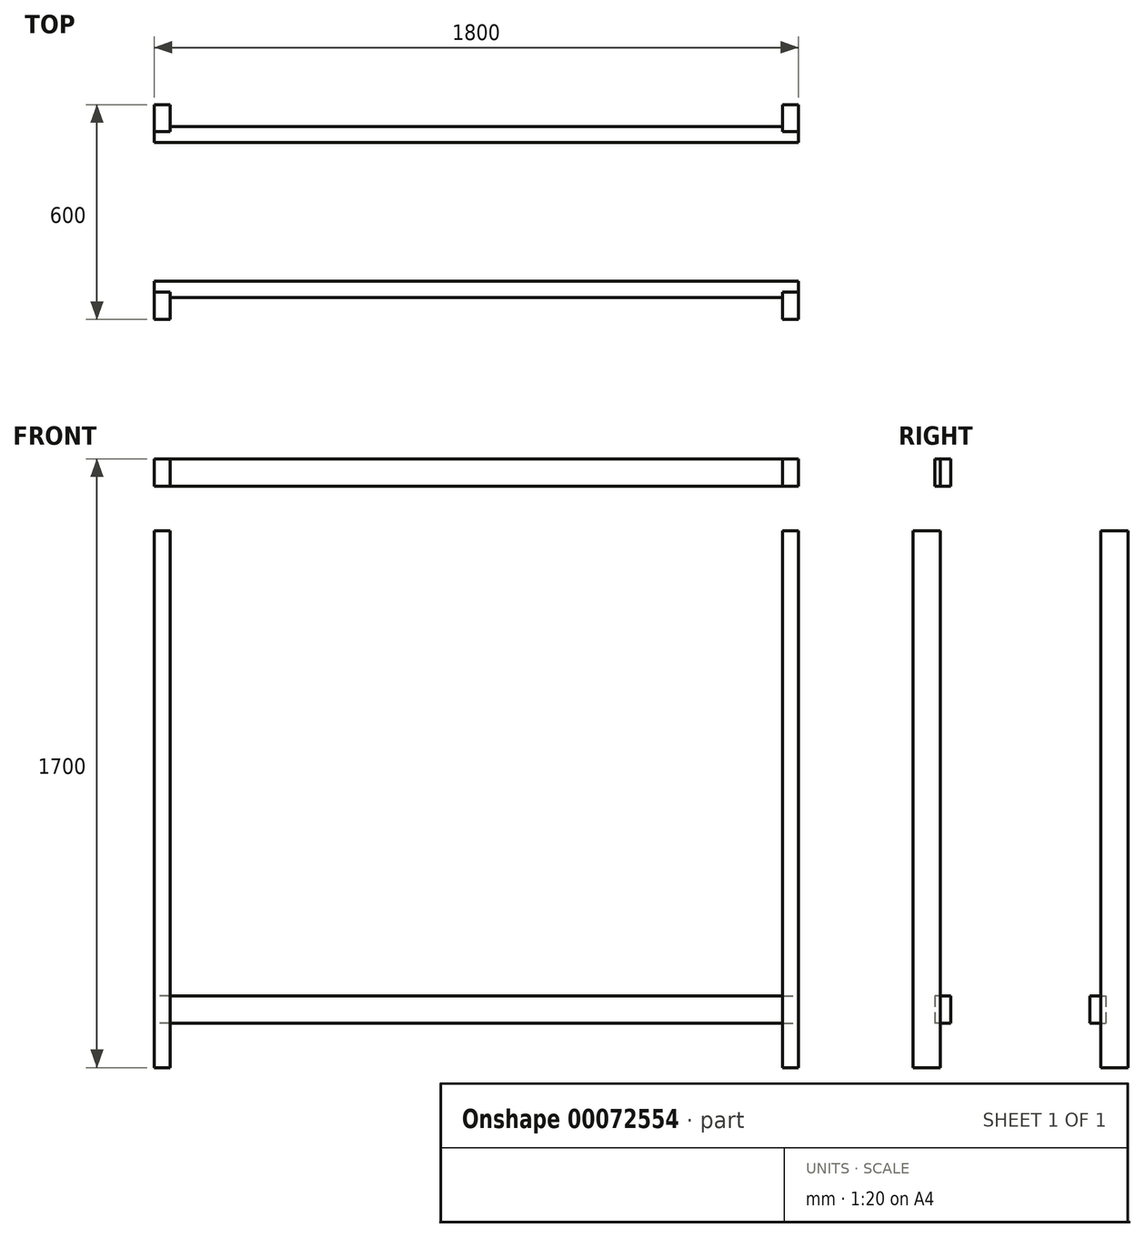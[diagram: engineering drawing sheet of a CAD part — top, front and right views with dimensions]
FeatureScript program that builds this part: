
annotation { "Feature Type Name" : "Feature", "Feature Type Description" : "" }
export const myFeature = defineFeature(function(context is Context, id is Id, definition is map)
    precondition{}
    {
        {
            var Q0;
            Q0=qCreatedBy(makeId("Top.planeOp"),FACE);
            var sketch = newSketch(context, id + "F0", { "sketchPlane" : qUnion([Q0])});
            skLineSegment(sketch, "E0.bottom", {"start": v(0, 0) * mm, "end": v(1800, 0) * mm, "construction": true});
            skLineSegment(sketch, "E0.top", {"start": v(0, -600) * mm, "end": v(1800, -600) * mm, "construction": true});
            skLineSegment(sketch, "E0.left", {"start": v(0, 0) * mm, "end": v(0, -600) * mm, "construction": true});
            skLineSegment(sketch, "E0.right", {"start": v(1800, 0) * mm, "end": v(1800, -600) * mm, "construction": true});
            skSolve(sketch);
        }
        {
            var Q0;
            Q0=qCreatedBy(makeId("Top.planeOp"),FACE);
            var sketch = newSketch(context, id + "F1", { "sketchPlane" : qUnion([Q0])});
            skLineSegment(sketch, "E1.bottom", {"start": v(0, 0) * mm, "end": v(45, 0) * mm});
            skLineSegment(sketch, "E1.top", {"start": v(0, -76) * mm, "end": v(45, -76) * mm});
            skLineSegment(sketch, "E1.left", {"start": v(0, 0) * mm, "end": v(0, -76) * mm});
            skLineSegment(sketch, "E1.right", {"start": v(45, 0) * mm, "end": v(45, -76) * mm});
            skLineSegment(sketch, "E2", {"start": v(0, -300) * mm, "end": v(1800, -300) * mm, "construction": true});
            skLineSegment(sketch, "E3.MirrorCS", {"start": v(0, -600) * mm, "end": v(0, -524) * mm});
            skLineSegment(sketch, "E4.MirrorCS", {"start": v(0, -600) * mm, "end": v(45, -600) * mm});
            skLineSegment(sketch, "E5.MirrorCS", {"start": v(0, -524) * mm, "end": v(45, -524) * mm});
            skLineSegment(sketch, "E6.MirrorCS", {"start": v(45, -600) * mm, "end": v(45, -524) * mm});
            skLineSegment(sketch, "E7", {"start": v(900, 0) * mm, "end": v(900, -600) * mm, "construction": true});
            skLineSegment(sketch, "E8.MirrorCS", {"start": v(1800, -76) * mm, "end": v(1755, -76) * mm});
            skLineSegment(sketch, "E9.MirrorCS", {"start": v(1755, 0) * mm, "end": v(1755, -76) * mm});
            skLineSegment(sketch, "E10.MirrorCS", {"start": v(1800, 0) * mm, "end": v(1755, 0) * mm});
            skLineSegment(sketch, "E11.MirrorCS", {"start": v(1800, 0) * mm, "end": v(1800, -76) * mm});
            skLineSegment(sketch, "E12.MirrorCS", {"start": v(1755, -600) * mm, "end": v(1755, -524) * mm});
            skLineSegment(sketch, "E13.MirrorCS", {"start": v(1800, -524) * mm, "end": v(1755, -524) * mm});
            skLineSegment(sketch, "E14.MirrorCS", {"start": v(1800, -600) * mm, "end": v(1800, -524) * mm});
            skLineSegment(sketch, "E15.MirrorCS", {"start": v(1800, -600) * mm, "end": v(1755, -600) * mm});
            skSolve(sketch);
        }
        {
            var Q0;
            Q0 = qSketchRegion(id + "F1", true);
            extrude(context, id + "F2", {"entities" : qUnion([Q0]), "depth" : 1500 * mm});
        }
        {
            var Q0;
            Q0=makeQuery(id+"F2.opExtrude","SWEPT_FACE",FACE,{"disambiguationData":[OSD([sQuery(id+"F1.wireOp",EDGE,"E14.MirrorCS")])]});
            var sketch = newSketch(context, id + "F3", { "sketchPlane" : qUnion([Q0])});
            skLineSegment(sketch, "E16.bottom", {"start": v(-539, 124) * mm, "end": v(-494, 124) * mm});
            skLineSegment(sketch, "E16.top", {"start": v(-539, 200) * mm, "end": v(-494, 200) * mm});
            skLineSegment(sketch, "E16.left", {"start": v(-539, 124) * mm, "end": v(-539, 200) * mm});
            skLineSegment(sketch, "E16.right", {"start": v(-494, 124) * mm, "end": v(-494, 200) * mm});
            skSolve(sketch);
        }
        {
            var Q0;
            {var subQ0=sQuery(id+"F3.wireOp",EDGE,"E16.right");Q0=makeQuery(id+"F3.imprint","IMPRINT",FACE,{"disambiguationData":[TD([[makeQuery(id+"F3.imprint","IMPRINT",EDGE,{"derivedFrom":subQ0}),1.0]])]});}
            var Q1;
            {var subQ0=sQuery(id+"F3.wireOp",EDGE,"E16.left");Q1=makeQuery(id+"F3.imprint","IMPRINT",FACE,{"disambiguationData":[TD([[makeQuery(id+"F3.imprint","IMPRINT",EDGE,{"derivedFrom":subQ0}),-1.0]])]});}
            extrude(context, id + "F4", {"entities" : qUnion([Q0, Q1]), "oppositeDirection" : true, "depth" : 1800 * mm});
        }
        {
            var Q0;
            Q0=makeQuery(id+"F4.opExtrude","SWEPT_FACE",FACE,{"disambiguationData":[OSD([sQuery(id+"F3.wireOp",EDGE,"E16.right")])]});
            var Q1;
            Q1=sQuery(id+"F1.wireOp",VERTEX,"E2.start");
            cPlane(context, id + "F5", {"entities" : qUnion([Q0, Q1]), "cplaneType" : CPlaneType.PLANE_POINT, "offset" : 152.4 * mm, "width" : 152.4 * mm, "height" : 152.4 * mm});
        }
        {
            var Q0;
            Q0=makeQuery(id+"F4.opExtrude","SWEPT_BODY",BODY,{"disambiguationData":[OSD([sQuery(id+"F3.wireOp",EDGE,"E16.bottom"),sQuery(id+"F3.wireOp",EDGE,"E16.top"),sQuery(id+"F3.wireOp",EDGE,"E16.left"),sQuery(id+"F3.wireOp",EDGE,"E16.right")])]});
            var Q1;
            Q1=qCreatedBy(id+"F5.planeOp",FACE);
            mirror(context, id + "F6", {"entities" : qUnion([Q0]), "mirrorPlane" : qUnion([Q1])});
        }
        {
            var Q0;
            Q0=makeQuery(id+"F2.opExtrude","SWEPT_BODY",BODY,{"disambiguationData":[OSD([sQuery(id+"F1.wireOp",EDGE,"E8.MirrorCS"),sQuery(id+"F1.wireOp",EDGE,"E9.MirrorCS"),sQuery(id+"F1.wireOp",EDGE,"E10.MirrorCS"),sQuery(id+"F1.wireOp",EDGE,"E11.MirrorCS")])]});
            var Q1;
            Q1=makeQuery(id+"F6.opPattern","COPY",BODY,{"derivedFrom":makeQuery(id+"F4.opExtrude","SWEPT_BODY",BODY,{"disambiguationData":[OSD([sQuery(id+"F3.wireOp",EDGE,"E16.bottom"),sQuery(id+"F3.wireOp",EDGE,"E16.top"),sQuery(id+"F3.wireOp",EDGE,"E16.left"),sQuery(id+"F3.wireOp",EDGE,"E16.right")])]}),"instanceName":"1"});
            booleanBodies(context, id + "F7", {"operationType" : BooleanOperationType.INTERSECTION, "tools" : qUnion([Q0, Q1]), "keepTools" : true});
        }
        {
            var Q0;
            Q0=makeQuery(id+"F7.opBoolean","INTERSECT",BODY,{"derivedFrom":[makeQuery(id+"F2.opExtrude","SWEPT_BODY",BODY,{"disambiguationData":[OSD([sQuery(id+"F1.wireOp",EDGE,"E8.MirrorCS"),sQuery(id+"F1.wireOp",EDGE,"E9.MirrorCS"),sQuery(id+"F1.wireOp",EDGE,"E10.MirrorCS"),sQuery(id+"F1.wireOp",EDGE,"E11.MirrorCS")])]}),makeQuery(id+"F6.opPattern","COPY",BODY,{"derivedFrom":makeQuery(id+"F4.opExtrude","SWEPT_BODY",BODY,{"disambiguationData":[OSD([sQuery(id+"F3.wireOp",EDGE,"E16.bottom"),sQuery(id+"F3.wireOp",EDGE,"E16.top"),sQuery(id+"F3.wireOp",EDGE,"E16.left"),sQuery(id+"F3.wireOp",EDGE,"E16.right")])]}),"instanceName":"1"})]});
            var Q1;
            Q1=makeQuery(id+"F6.opPattern","COPY",BODY,{"derivedFrom":makeQuery(id+"F4.opExtrude","SWEPT_BODY",BODY,{"disambiguationData":[OSD([sQuery(id+"F3.wireOp",EDGE,"E16.bottom"),sQuery(id+"F3.wireOp",EDGE,"E16.top"),sQuery(id+"F3.wireOp",EDGE,"E16.left"),sQuery(id+"F3.wireOp",EDGE,"E16.right")])]}),"instanceName":"1"});
            booleanBodies(context, id + "F8", {"operationType" : BooleanOperationType.SUBTRACTION, "tools" : qUnion([Q0]), "targets" : qUnion([Q1]), "keepTools" : true});
        }
        {
            var Q0;
            Q0=makeQuery(id+"F2.opExtrude","SWEPT_FACE",FACE,{"disambiguationData":[OSD([sQuery(id+"F1.wireOp",EDGE,"E1.right")])]});
            var Q1;
            Q1=sQuery(id+"F1.wireOp",VERTEX,"E7.end");
            cPlane(context, id + "F9", {"entities" : qUnion([Q0, Q1]), "cplaneType" : CPlaneType.PLANE_POINT, "offset" : 150 * mm, "width" : 150 * mm, "height" : 150 * mm});
        }
        {
            var Q0;
            Q0=makeQuery(id+"F7.opBoolean","INTERSECT",BODY,{"derivedFrom":[makeQuery(id+"F2.opExtrude","SWEPT_BODY",BODY,{"disambiguationData":[OSD([sQuery(id+"F1.wireOp",EDGE,"E8.MirrorCS"),sQuery(id+"F1.wireOp",EDGE,"E9.MirrorCS"),sQuery(id+"F1.wireOp",EDGE,"E10.MirrorCS"),sQuery(id+"F1.wireOp",EDGE,"E11.MirrorCS")])]}),makeQuery(id+"F6.opPattern","COPY",BODY,{"derivedFrom":makeQuery(id+"F4.opExtrude","SWEPT_BODY",BODY,{"disambiguationData":[OSD([sQuery(id+"F3.wireOp",EDGE,"E16.bottom"),sQuery(id+"F3.wireOp",EDGE,"E16.top"),sQuery(id+"F3.wireOp",EDGE,"E16.left"),sQuery(id+"F3.wireOp",EDGE,"E16.right")])]}),"instanceName":"1"})]});
            var Q1;
            Q1=qCreatedBy(id+"F9.planeOp",FACE);
            mirror(context, id + "F10", {"entities" : qUnion([Q0]), "mirrorPlane" : qUnion([Q1])});
        }
        {
            var Q0;
            Q0=makeQuery(id+"F10.opPattern","COPY",BODY,{"derivedFrom":makeQuery(id+"F7.opBoolean","INTERSECT",BODY,{"derivedFrom":[makeQuery(id+"F2.opExtrude","SWEPT_BODY",BODY,{"disambiguationData":[OSD([sQuery(id+"F1.wireOp",EDGE,"E8.MirrorCS"),sQuery(id+"F1.wireOp",EDGE,"E9.MirrorCS"),sQuery(id+"F1.wireOp",EDGE,"E10.MirrorCS"),sQuery(id+"F1.wireOp",EDGE,"E11.MirrorCS")])]}),makeQuery(id+"F6.opPattern","COPY",BODY,{"derivedFrom":makeQuery(id+"F4.opExtrude","SWEPT_BODY",BODY,{"disambiguationData":[OSD([sQuery(id+"F3.wireOp",EDGE,"E16.bottom"),sQuery(id+"F3.wireOp",EDGE,"E16.top"),sQuery(id+"F3.wireOp",EDGE,"E16.left"),sQuery(id+"F3.wireOp",EDGE,"E16.right")])]}),"instanceName":"1"})]}),"instanceName":"1"});
            var Q1;
            Q1=makeQuery(id+"F7.opBoolean","INTERSECT",BODY,{"derivedFrom":[makeQuery(id+"F2.opExtrude","SWEPT_BODY",BODY,{"disambiguationData":[OSD([sQuery(id+"F1.wireOp",EDGE,"E8.MirrorCS"),sQuery(id+"F1.wireOp",EDGE,"E9.MirrorCS"),sQuery(id+"F1.wireOp",EDGE,"E10.MirrorCS"),sQuery(id+"F1.wireOp",EDGE,"E11.MirrorCS")])]}),makeQuery(id+"F6.opPattern","COPY",BODY,{"derivedFrom":makeQuery(id+"F4.opExtrude","SWEPT_BODY",BODY,{"disambiguationData":[OSD([sQuery(id+"F3.wireOp",EDGE,"E16.bottom"),sQuery(id+"F3.wireOp",EDGE,"E16.top"),sQuery(id+"F3.wireOp",EDGE,"E16.left"),sQuery(id+"F3.wireOp",EDGE,"E16.right")])]}),"instanceName":"1"})]});
            var Q2;
            Q2=qCreatedBy(id+"F5.planeOp",FACE);
            mirror(context, id + "F11", {"entities" : qUnion([Q0, Q1]), "mirrorPlane" : qUnion([Q2])});
        }
        {
            var Q0;
            Q0=makeQuery(id+"F11.opPattern","COPY",BODY,{"derivedFrom":makeQuery(id+"F10.opPattern","COPY",BODY,{"derivedFrom":makeQuery(id+"F7.opBoolean","INTERSECT",BODY,{"derivedFrom":[makeQuery(id+"F2.opExtrude","SWEPT_BODY",BODY,{"disambiguationData":[OSD([sQuery(id+"F1.wireOp",EDGE,"E8.MirrorCS"),sQuery(id+"F1.wireOp",EDGE,"E9.MirrorCS"),sQuery(id+"F1.wireOp",EDGE,"E10.MirrorCS"),sQuery(id+"F1.wireOp",EDGE,"E11.MirrorCS")])]}),makeQuery(id+"F6.opPattern","COPY",BODY,{"derivedFrom":makeQuery(id+"F4.opExtrude","SWEPT_BODY",BODY,{"disambiguationData":[OSD([sQuery(id+"F3.wireOp",EDGE,"E16.bottom"),sQuery(id+"F3.wireOp",EDGE,"E16.top"),sQuery(id+"F3.wireOp",EDGE,"E16.left"),sQuery(id+"F3.wireOp",EDGE,"E16.right")])]}),"instanceName":"1"})]}),"instanceName":"1"}),"instanceName":"1"});
            var Q1;
            Q1=makeQuery(id+"F11.opPattern","COPY",BODY,{"derivedFrom":makeQuery(id+"F7.opBoolean","INTERSECT",BODY,{"derivedFrom":[makeQuery(id+"F2.opExtrude","SWEPT_BODY",BODY,{"disambiguationData":[OSD([sQuery(id+"F1.wireOp",EDGE,"E8.MirrorCS"),sQuery(id+"F1.wireOp",EDGE,"E9.MirrorCS"),sQuery(id+"F1.wireOp",EDGE,"E10.MirrorCS"),sQuery(id+"F1.wireOp",EDGE,"E11.MirrorCS")])]}),makeQuery(id+"F6.opPattern","COPY",BODY,{"derivedFrom":makeQuery(id+"F4.opExtrude","SWEPT_BODY",BODY,{"disambiguationData":[OSD([sQuery(id+"F3.wireOp",EDGE,"E16.bottom"),sQuery(id+"F3.wireOp",EDGE,"E16.top"),sQuery(id+"F3.wireOp",EDGE,"E16.left"),sQuery(id+"F3.wireOp",EDGE,"E16.right")])]}),"instanceName":"1"})]}),"instanceName":"1"});
            var Q2;
            Q2=makeQuery(id+"F10.opPattern","COPY",BODY,{"derivedFrom":makeQuery(id+"F7.opBoolean","INTERSECT",BODY,{"derivedFrom":[makeQuery(id+"F2.opExtrude","SWEPT_BODY",BODY,{"disambiguationData":[OSD([sQuery(id+"F1.wireOp",EDGE,"E8.MirrorCS"),sQuery(id+"F1.wireOp",EDGE,"E9.MirrorCS"),sQuery(id+"F1.wireOp",EDGE,"E10.MirrorCS"),sQuery(id+"F1.wireOp",EDGE,"E11.MirrorCS")])]}),makeQuery(id+"F6.opPattern","COPY",BODY,{"derivedFrom":makeQuery(id+"F4.opExtrude","SWEPT_BODY",BODY,{"disambiguationData":[OSD([sQuery(id+"F3.wireOp",EDGE,"E16.bottom"),sQuery(id+"F3.wireOp",EDGE,"E16.top"),sQuery(id+"F3.wireOp",EDGE,"E16.left"),sQuery(id+"F3.wireOp",EDGE,"E16.right")])]}),"instanceName":"1"})]}),"instanceName":"1"});
            var Q3;
            Q3=makeQuery(id+"F7.opBoolean","INTERSECT",BODY,{"derivedFrom":[makeQuery(id+"F2.opExtrude","SWEPT_BODY",BODY,{"disambiguationData":[OSD([sQuery(id+"F1.wireOp",EDGE,"E8.MirrorCS"),sQuery(id+"F1.wireOp",EDGE,"E9.MirrorCS"),sQuery(id+"F1.wireOp",EDGE,"E10.MirrorCS"),sQuery(id+"F1.wireOp",EDGE,"E11.MirrorCS")])]}),makeQuery(id+"F6.opPattern","COPY",BODY,{"derivedFrom":makeQuery(id+"F4.opExtrude","SWEPT_BODY",BODY,{"disambiguationData":[OSD([sQuery(id+"F3.wireOp",EDGE,"E16.bottom"),sQuery(id+"F3.wireOp",EDGE,"E16.top"),sQuery(id+"F3.wireOp",EDGE,"E16.left"),sQuery(id+"F3.wireOp",EDGE,"E16.right")])]}),"instanceName":"1"})]});
            var Q4;
            Q4=makeQuery(id+"F4.opExtrude","SWEPT_BODY",BODY,{"disambiguationData":[OSD([sQuery(id+"F3.wireOp",EDGE,"E16.bottom"),sQuery(id+"F3.wireOp",EDGE,"E16.top"),sQuery(id+"F3.wireOp",EDGE,"E16.left"),sQuery(id+"F3.wireOp",EDGE,"E16.right")])]});
            var Q5;
            Q5=makeQuery(id+"F6.opPattern","COPY",BODY,{"derivedFrom":makeQuery(id+"F4.opExtrude","SWEPT_BODY",BODY,{"disambiguationData":[OSD([sQuery(id+"F3.wireOp",EDGE,"E16.bottom"),sQuery(id+"F3.wireOp",EDGE,"E16.top"),sQuery(id+"F3.wireOp",EDGE,"E16.left"),sQuery(id+"F3.wireOp",EDGE,"E16.right")])]}),"instanceName":"1"});
            booleanBodies(context, id + "F12", {"operationType" : BooleanOperationType.SUBTRACTION, "tools" : qUnion([Q0, Q1, Q2, Q3]), "targets" : qUnion([Q4, Q5])});
        }
        {
            var Q0;
            Q0=makeQuery(id+"F4.opExtrude","SWEPT_BODY",BODY,{"disambiguationData":[OSD([sQuery(id+"F3.wireOp",EDGE,"E16.bottom"),sQuery(id+"F3.wireOp",EDGE,"E16.top"),sQuery(id+"F3.wireOp",EDGE,"E16.left"),sQuery(id+"F3.wireOp",EDGE,"E16.right")])]});
            transform(context, id + "F13", {"entities" : qUnion([Q0]), "transformType" : TransformType.TRANSLATION_3D, "dx" : 0 * mm, "dy" : 0 * mm, "dz" : 0 * mm, "makeCopy" : true});
        }
        {
            var Q0;
            Q0=makeQuery(id+"F13.opPattern","COPY",BODY,{"derivedFrom":makeQuery(id+"F4.opExtrude","SWEPT_BODY",BODY,{"disambiguationData":[OSD([sQuery(id+"F3.wireOp",EDGE,"E16.bottom"),sQuery(id+"F3.wireOp",EDGE,"E16.top"),sQuery(id+"F3.wireOp",EDGE,"E16.left"),sQuery(id+"F3.wireOp",EDGE,"E16.right")])]}),"instanceName":"1"});
            transform(context, id + "F14", {"entities" : qUnion([Q0]), "transformType" : TransformType.TRANSLATION_3D, "dx" : 0 * mm, "dy" : 0 * mm, "dz" : 1500 * mm, "makeCopy" : true});
        }
        {
            var Q0;
            Q0=makeQuery(id+"F13.opPattern","COPY",BODY,{"derivedFrom":makeQuery(id+"F4.opExtrude","SWEPT_BODY",BODY,{"disambiguationData":[OSD([sQuery(id+"F3.wireOp",EDGE,"E16.bottom"),sQuery(id+"F3.wireOp",EDGE,"E16.top"),sQuery(id+"F3.wireOp",EDGE,"E16.left"),sQuery(id+"F3.wireOp",EDGE,"E16.right")])]}),"instanceName":"1"});
            deleteBodies(context, id + "F15", {"entities" : qUnion([Q0])});
        }
    });
